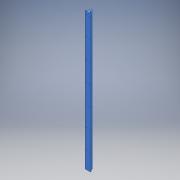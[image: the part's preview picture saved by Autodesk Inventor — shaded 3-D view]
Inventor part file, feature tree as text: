
AUTODESK INVENTOR PART (.ipt)
format: ipt  version: 2018 (Build 220112000, 112)  size: 159,744 bytes
history: native  units: mm
features: other x1, extrude x1, hole x1, sketch x1
ambient origin geometry x8: Origin, YZ Plane, XZ Plane, XY Plane, X Axis, Y Axis, Z Axis, Center Point
bodies: Body1 (feature_tree)
feature tree (4):
  other  "Sólido1"
  extrude  "Extrusão1"  Depth=8.0mm
  hole  "Furo2"  [1 undecoded]
  sketch  "Esboço1"  dims[d6=16.0mm d7=25.0mm d8=18.5mm d9=11.7mm d10=8.0mm d11=30.0deg d12=30.0deg d13=5.0mm d14=40.0mm d15=1054.0mm d16=0.0mm d18=15.0mm d19=15.0mm d20=5.5mm d21=5.5mm d22=25.0mm d39=150.0mm d44=5.5mm d45=6.0mm d46=4.0mm d47=2.0mm d48=90.0deg d49=8.0mm d50=20.594885mm]
note: 1 required parameter value undecoded (feature->parameter linkage not recoverable at this tier; creation-order binding heuristic only, values carry confidence <= 0.55)
